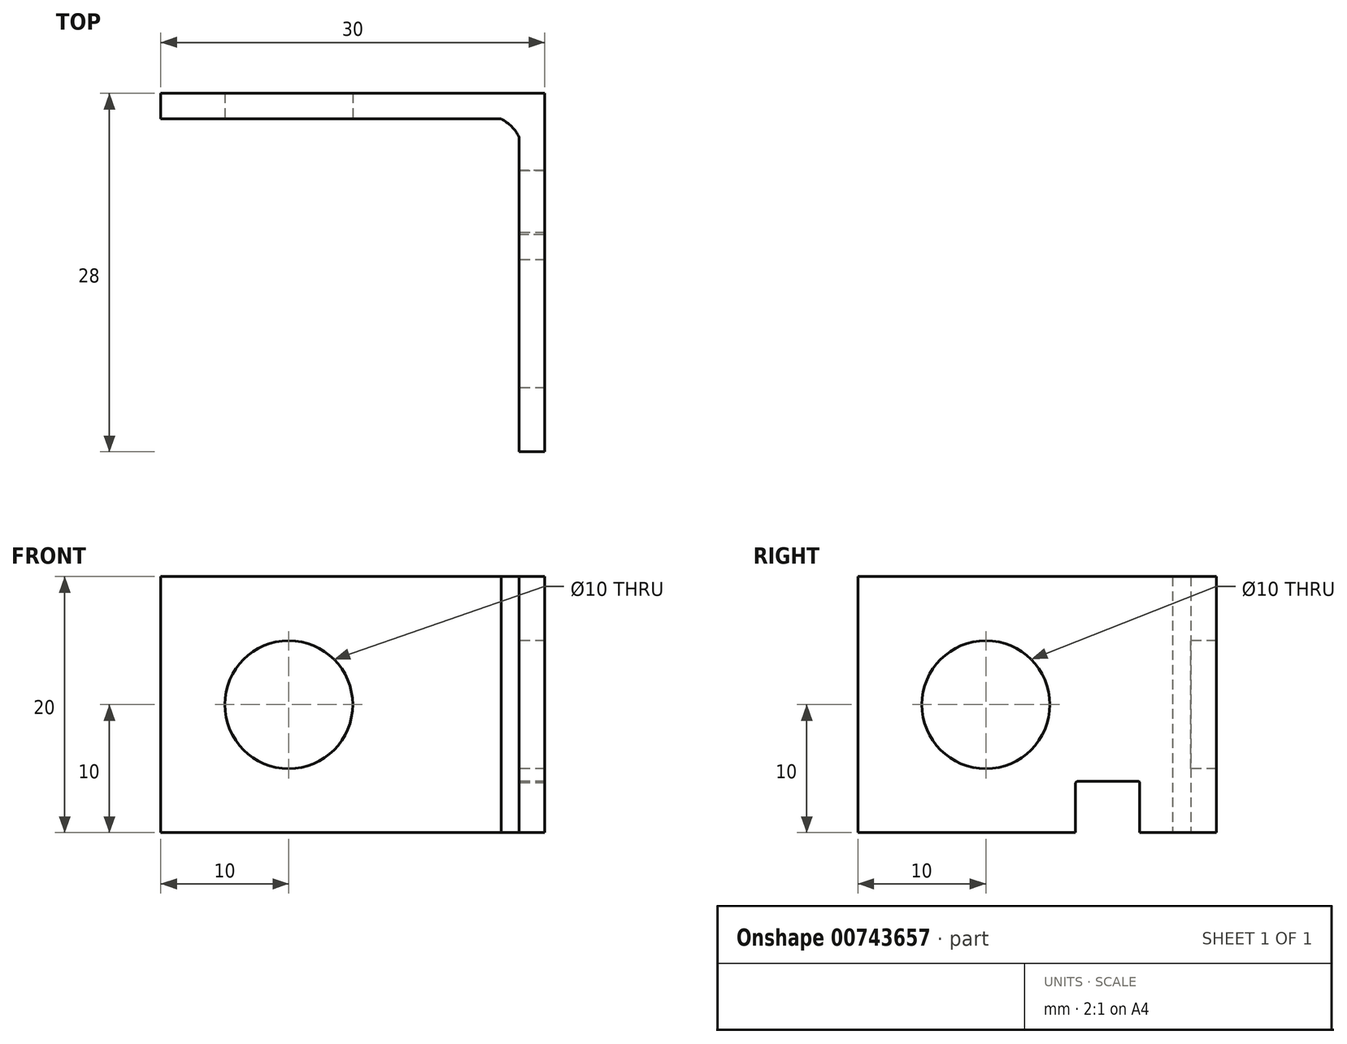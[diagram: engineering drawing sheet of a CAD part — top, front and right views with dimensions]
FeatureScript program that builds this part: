
annotation { "Feature Type Name" : "Feature", "Feature Type Description" : "" }
export const myFeature = defineFeature(function(context is Context, id is Id, definition is map)
    precondition{}
    {
        {
            var Q0;
            Q0=qCreatedBy(makeId("Front.planeOp"),FACE);
            var sketch = newSketch(context, id + "F0", { "sketchPlane" : qUnion([Q0])});
            skLineSegment(sketch, "E0.bottom", {"start": v(0, 0) * mm, "end": v(30, 0) * mm});
            skLineSegment(sketch, "E0.top", {"start": v(0, -20) * mm, "end": v(30, -20) * mm});
            skLineSegment(sketch, "E0.left", {"start": v(0, 0) * mm, "end": v(0, -20) * mm});
            skLineSegment(sketch, "E0.right", {"start": v(30, 0) * mm, "end": v(30, -20) * mm});
            skPoint(sketch, "E1.firstSnap0", {"position": v(15, 0) * mm});
            skSolve(sketch);
        }
        {
            var Q0;
            Q0 = qSketchRegion(id + "F0", true);
            extrude(context, id + "F1", {"entities" : qUnion([Q0]), "depth" : 2 * mm, "offsetDistance" : 25 * mm});
        }
        {
            var Q0;
            Q0=makeQuery(id+"F1.opExtrude","CAP_FACE",FACE,{"disambiguationData":[OSD([sQuery(id+"F0.wireOp",EDGE,"E0.bottom"),sQuery(id+"F0.wireOp",EDGE,"E0.top"),sQuery(id+"F0.wireOp",EDGE,"E0.left"),sQuery(id+"F0.wireOp",EDGE,"E0.right")])],"isStart":false});
            var sketch = newSketch(context, id + "F2", { "sketchPlane" : qUnion([Q0])});
            skCircle(sketch, "E2", {"center": v(10, -10) * mm, "radius": 5 * mm});
            skSolve(sketch);
        }
        {
            var Q0;
            Q0 = qSketchRegion(id + "F2", true);
            extrude(context, id + "F3", {"entities" : qUnion([Q0]), "operationType" : NewBodyOperationType.REMOVE, "oppositeDirection" : true, "depth" : 25 * mm, "offsetDistance" : 25 * mm});
        }
        {
            var Q0;
            Q0=makeQuery(id+"F1.opExtrude","SWEPT_FACE",FACE,{"disambiguationData":[OSD([sQuery(id+"F0.wireOp",EDGE,"E0.right")])]});
            var sketch = newSketch(context, id + "F4", { "sketchPlane" : qUnion([Q0])});
            skLineSegment(sketch, "E3.bottom", {"start": v(-2, -20) * mm, "end": v(-28, -20) * mm});
            skLineSegment(sketch, "E3.top", {"start": v(-2, 0) * mm, "end": v(-28, 0) * mm});
            skLineSegment(sketch, "E3.left", {"start": v(-2, -20) * mm, "end": v(-2, 0) * mm});
            skLineSegment(sketch, "E3.right", {"start": v(-28, -20) * mm, "end": v(-28, 0) * mm});
            skLineSegment(sketch, "E4", {"start": v(-8, -20) * mm, "end": v(-8, -16) * mm});
            skLineSegment(sketch, "E5", {"start": v(-8, -16) * mm, "end": v(-3, -16) * mm});
            skLineSegment(sketch, "E6", {"start": v(-3, -16) * mm, "end": v(-3, -20) * mm});
            skSolve(sketch);
        }
        {
            var Q0;
            Q0 = qSketchRegion(id + "F4", true);
            extrude(context, id + "F5", {"entities" : qUnion([Q0]), "operationType" : NewBodyOperationType.ADD, "oppositeDirection" : true, "depth" : 2 * mm, "offsetDistance" : 25 * mm});
        }
        {
            var Q0;
            Q0=makeQuery(id+"F5.boolean.opBoolean","MERGE",FACE,{"derivedFrom":[makeQuery(id+"F1.opExtrude","SWEPT_FACE",FACE,{"disambiguationData":[OSD([sQuery(id+"F0.wireOp",EDGE,"E0.right")])]}),makeQuery(id+"F5.opExtrude","CAP_FACE",FACE,{"disambiguationData":[OSD([sQuery(id+"F4.wireOp",EDGE,"E3.bottom"),sQuery(id+"F4.wireOp",EDGE,"E3.top"),sQuery(id+"F4.wireOp",EDGE,"E3.left"),sQuery(id+"F4.wireOp",EDGE,"E3.right")])],"isStart":true})]});
            var sketch = newSketch(context, id + "F6", { "sketchPlane" : qUnion([Q0])});
            skLineSegment(sketch, "E7.bottom", {"start": v(-11, -20) * mm, "end": v(-6, -20) * mm});
            skLineSegment(sketch, "E7.top", {"start": v(-11, -16) * mm, "end": v(-6, -16) * mm});
            skLineSegment(sketch, "E7.left", {"start": v(-11, -20) * mm, "end": v(-11, -16) * mm});
            skLineSegment(sketch, "E7.right", {"start": v(-6, -20) * mm, "end": v(-6, -16) * mm});
            skSolve(sketch);
        }
        {
            var Q0;
            Q0=makeQuery(id+"F6.imprint","IMPRINT",FACE,{"disambiguationData":[TD([[makeQuery(id+"F6.imprint","IMPRINT",EDGE,{"derivedFrom":sQuery(id+"F6.wireOp",EDGE,"E7.bottom")}),1.0]])]});
            extrude(context, id + "F7", {"entities" : qUnion([Q0]), "operationType" : NewBodyOperationType.REMOVE, "oppositeDirection" : true, "depth" : 25 * mm, "offsetDistance" : 25 * mm});
        }
        {
            var Q0;
            Q0=makeQuery(id+"F5.opExtrude","CAP_FACE",FACE,{"disambiguationData":[OSD([sQuery(id+"F4.wireOp",EDGE,"E3.bottom"),sQuery(id+"F4.wireOp",EDGE,"E3.top"),sQuery(id+"F4.wireOp",EDGE,"E3.left"),sQuery(id+"F4.wireOp",EDGE,"E3.right")])],"isStart":false});
            var sketch = newSketch(context, id + "F8", { "sketchPlane" : qUnion([Q0])});
            skCircle(sketch, "E8", {"center": v(18, -10) * mm, "radius": 5 * mm});
            skSolve(sketch);
        }
        {
            var Q0;
            Q0 = qSketchRegion(id + "F8", true);
            extrude(context, id + "F9", {"entities" : qUnion([Q0]), "operationType" : NewBodyOperationType.REMOVE, "oppositeDirection" : true, "depth" : 25 * mm, "offsetDistance" : 25 * mm});
        }
        {
            var Q0;
            {var subQ1=sQuery(id+"F0.wireOp",EDGE,"E0.left");var subQ2=sQuery(id+"F0.wireOp",EDGE,"E0.top");var subQ7=sQuery(id+"F4.wireOp",EDGE,"E3.bottom");Q0=makeQuery(id+"F7.boolean.opBoolean","SPLIT",FACE,{"disambiguationData":[TD([makeQuery(id+"F1.opExtrude","SWEPT_FACE",FACE,{"disambiguationData":[OSD([subQ1])]})])],"derivedFrom":makeQuery(id+"F5.boolean.opBoolean","MERGE",FACE,{"derivedFrom":[makeQuery(id+"F1.opExtrude","SWEPT_FACE",FACE,{"disambiguationData":[OSD([subQ2])]}),makeQuery(id+"F5.opExtrude","SWEPT_FACE",FACE,{"disambiguationData":[OSD([subQ7])]})]})});}
            var sketch = newSketch(context, id + "F10", { "sketchPlane" : qUnion([Q0])});
            skLineSegment(sketch, "E9", {"start": v(24, 2) * mm, "end": v(24, 0) * mm});
            skLineSegment(sketch, "E10", {"start": v(24, 0) * mm, "end": v(30, 0) * mm});
            skLineSegment(sketch, "E11", {"start": v(30, 0) * mm, "end": v(30, 6) * mm});
            skLineSegment(sketch, "E12", {"start": v(30, 6) * mm, "end": v(28, 6) * mm});
            skArc(sketch, "E13", {"start": v(24, 2) * mm, "mid": v(27.41, 2.59) * mm, "end": v(28, 6) * mm});
            skSolve(sketch);
        }
        {
            var Q0;
            Q0 = qSketchRegion(id + "F10", true);
            extrude(context, id + "F11", {"entities" : qUnion([Q0]), "operationType" : NewBodyOperationType.ADD, "oppositeDirection" : true, "depth" : 20 * mm, "offsetDistance" : 25 * mm});
        }
        {
            var Q0;
            Q0=makeQuery(id+"F5.opExtrude","CAP_FACE",FACE,{"disambiguationData":[OSD([sQuery(id+"F4.wireOp",EDGE,"E3.bottom"),sQuery(id+"F4.wireOp",EDGE,"E3.top"),sQuery(id+"F4.wireOp",EDGE,"E3.left"),sQuery(id+"F4.wireOp",EDGE,"E3.right")])],"isStart":false});
            var sketch = newSketch(context, id + "F12", { "sketchPlane" : qUnion([Q0])});
            skLineSegment(sketch, "E14", {"start": v(10.88, -16) * mm, "end": v(11, -16.12) * mm});
            skLineSegment(sketch, "E15", {"start": v(10.88, -16) * mm, "end": v(11, -16) * mm});
            skLineSegment(sketch, "E16", {"start": v(11, -16) * mm, "end": v(11, -16.12) * mm});
            skSolve(sketch);
        }
        {
            var Q0;
            Q0 = qSketchRegion(id + "F12", true);
            extrude(context, id + "F13", {"entities" : qUnion([Q0]), "operationType" : NewBodyOperationType.ADD, "oppositeDirection" : true, "depth" : 2 * mm, "offsetDistance" : 25 * mm});
        }
        {
            var Q0;
            Q0=makeQuery(id+"F13.boolean.opBoolean","MERGE",FACE,{"derivedFrom":[makeQuery(id+"F5.opExtrude","CAP_FACE",FACE,{"disambiguationData":[OSD([sQuery(id+"F4.wireOp",EDGE,"E3.bottom"),sQuery(id+"F4.wireOp",EDGE,"E3.top"),sQuery(id+"F4.wireOp",EDGE,"E3.left"),sQuery(id+"F4.wireOp",EDGE,"E3.right")])],"isStart":false}),makeQuery(id+"F13.opExtrude","CAP_FACE",FACE,{"disambiguationData":[OSD([sQuery(id+"F12.wireOp",EDGE,"E14"),sQuery(id+"F12.wireOp",EDGE,"E15"),sQuery(id+"F12.wireOp",EDGE,"E16")])],"isStart":true})]});
            var sketch = newSketch(context, id + "F14", { "sketchPlane" : qUnion([Q0])});
            skLineSegment(sketch, "E17", {"start": v(6, -16) * mm, "end": v(6.06, -16) * mm});
            skLineSegment(sketch, "E18", {"start": v(6.06, -16) * mm, "end": v(6, -16.06) * mm});
            skLineSegment(sketch, "E19", {"start": v(6, -16.06) * mm, "end": v(6, -16) * mm});
            skSolve(sketch);
        }
        {
            var Q0;
            Q0 = qSketchRegion(id + "F14", true);
            extrude(context, id + "F15", {"entities" : qUnion([Q0]), "operationType" : NewBodyOperationType.ADD, "oppositeDirection" : true, "depth" : 2 * mm, "offsetDistance" : 25 * mm});
        }
    });
